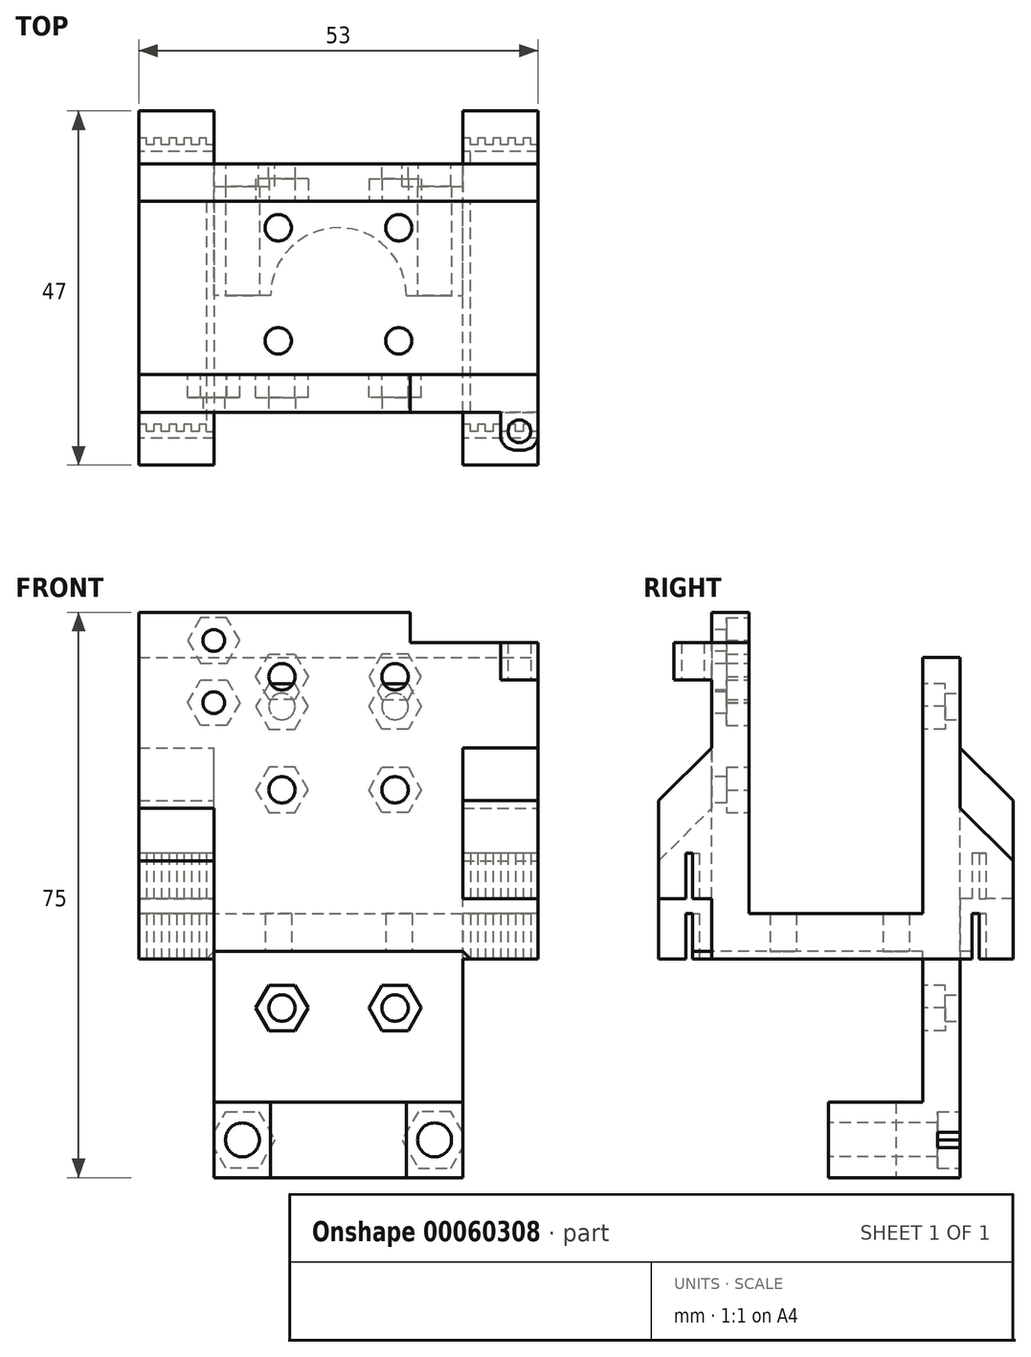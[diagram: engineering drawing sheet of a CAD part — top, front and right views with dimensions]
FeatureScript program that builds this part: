
annotation { "Feature Type Name" : "Feature", "Feature Type Description" : "" }
export const myFeature = defineFeature(function(context is Context, id is Id, definition is map)
    precondition{}
    {
        {
            var Q0;
            Q0=qCreatedBy(makeId("Top.planeOp"),FACE);
            var sketch = newSketch(context, id + "F0", { "sketchPlane" : qUnion([Q0]), "disableImprinting" : false});
            skLineSegment(sketch, "E0.bottom", {"start": v(-26.5, 16) * mm, "end": v(26.5, 16) * mm});
            skLineSegment(sketch, "E0.top", {"start": v(-26.5, -17) * mm, "end": v(26.5, -17) * mm});
            skLineSegment(sketch, "E0.left", {"start": v(-26.5, 16) * mm, "end": v(-26.5, -17) * mm});
            skLineSegment(sketch, "E0.right", {"start": v(26.5, 16) * mm, "end": v(26.5, -17) * mm});
            skLineSegment(sketch, "E1", {"start": v(0, 16) * mm, "end": v(0, -17) * mm, "construction": true});
            skCircle(sketch, "E2", {"center": v(-8, -7.5) * mm, "radius": 1.75 * mm});
            skCircle(sketch, "E3", {"center": v(8, -7.5) * mm, "radius": 1.75 * mm});
            skLineSegment(sketch, "E4", {"start": v(-26.5, -7.5) * mm, "end": v(26.5, -7.5) * mm, "construction": true});
            skLineSegment(sketch, "E5", {"start": v(-26.5, 7.5) * mm, "end": v(26.5, 7.5) * mm, "construction": true});
            skCircle(sketch, "E6", {"center": v(-8, 7.5) * mm, "radius": 1.75 * mm});
            skCircle(sketch, "E7", {"center": v(8, 7.5) * mm, "radius": 1.75 * mm});
            skLineSegment(sketch, "E8", {"start": v(26.5, -0.5) * mm, "end": v(-26.5, -0.5) * mm, "construction": true});
            skLineSegment(sketch, "E9", {"start": v(8, 16) * mm, "end": v(8, -17) * mm, "construction": true});
            skLineSegment(sketch, "E10", {"start": v(-8, 16) * mm, "end": v(-8, -17) * mm, "construction": true});
            skSolve(sketch);
        }
        {
            var Q0;
            Q0=makeQuery(id+"F0.imprint","IMPRINT",FACE,{"disambiguationData":[TD([[makeQuery(id+"F0.imprint","IMPRINT",EDGE,{"derivedFrom":sQuery(id+"F0.wireOp",EDGE,"E0.bottom")}),-1.0]])]});
            extrude(context, id + "F1", {"entities" : qUnion([Q0]), "depth" : 5 * mm});
        }
        {
            var Q0;
            Q0=makeQuery(id+"F1.opExtrude","CAP_FACE",FACE,{"disambiguationData":[OSD([sQuery(id+"F0.wireOp",EDGE,"E0.bottom"),sQuery(id+"F0.wireOp",EDGE,"E0.top"),sQuery(id+"F0.wireOp",EDGE,"E0.left"),sQuery(id+"F0.wireOp",EDGE,"E0.right"),sQuery(id+"F0.wireOp",EDGE,"E2"),sQuery(id+"F0.wireOp",EDGE,"E3"),sQuery(id+"F0.wireOp",EDGE,"E6"),sQuery(id+"F0.wireOp",EDGE,"E7")])],"isStart":false});
            var sketch = newSketch(context, id + "F2", { "sketchPlane" : qUnion([Q0])});
            skLineSegment(sketch, "E11.bottom", {"start": v(-26.5, 16) * mm, "end": v(26.5, 16) * mm});
            skLineSegment(sketch, "E11.top", {"start": v(-26.5, 11) * mm, "end": v(26.5, 11) * mm});
            skLineSegment(sketch, "E11.left", {"start": v(-26.5, 16) * mm, "end": v(-26.5, 11) * mm});
            skLineSegment(sketch, "E11.right", {"start": v(26.5, 16) * mm, "end": v(26.5, 11) * mm});
            skLineSegment(sketch, "E12.MirrorCS", {"start": v(-26.5, -12) * mm, "end": v(26.5, -12) * mm});
            skLineSegment(sketch, "E13.MirrorCS", {"start": v(-26.5, -17) * mm, "end": v(26.5, -17) * mm});
            skLineSegment(sketch, "E14.MirrorCS", {"start": v(26.5, -17) * mm, "end": v(26.5, -12) * mm});
            skLineSegment(sketch, "E15.MirrorCS", {"start": v(-26.5, -17) * mm, "end": v(-26.5, -12) * mm});
            skSolve(sketch);
        }
        {
            var Q0;
            Q0=makeQuery(id+"F2.imprint","IMPRINT",FACE,{"disambiguationData":[TD([[makeQuery(id+"F2.imprint","IMPRINT",EDGE,{"derivedFrom":sQuery(id+"F2.wireOp",EDGE,"E12.MirrorCS")}),-1.0]])]});
            extrude(context, id + "F3", {"entities" : qUnion([Q0]), "operationType" : NewBodyOperationType.ADD, "depth" : 40 * mm});
        }
        {
            var Q0;
            Q0=makeQuery(id+"F2.imprint","IMPRINT",FACE,{"disambiguationData":[TD([[makeQuery(id+"F2.imprint","IMPRINT",EDGE,{"derivedFrom":sQuery(id+"F2.wireOp",EDGE,"E11.bottom")}),-1.0]])]});
            extrude(context, id + "F4", {"entities" : qUnion([Q0]), "operationType" : NewBodyOperationType.ADD, "depth" : 34 * mm});
        }
        {
            var Q0;
            Q0=makeQuery(id+"F3.boolean.opBoolean","MERGE",FACE,{"derivedFrom":[makeQuery(id+"F1.opExtrude","SWEPT_FACE",FACE,{"disambiguationData":[OSD([sQuery(id+"F0.wireOp",EDGE,"E0.top")])]}),makeQuery(id+"F3.opExtrude","SWEPT_FACE",FACE,{"disambiguationData":[OSD([sQuery(id+"F2.wireOp",EDGE,"E13.MirrorCS")])]})]});
            var sketch = newSketch(context, id + "F5", { "sketchPlane" : qUnion([Q0])});
            skLineSegment(sketch, "E16.bottom", {"start": v(12.5, 0) * mm, "end": v(-12.5, 0) * mm});
            skLineSegment(sketch, "E16.top", {"start": v(12.5, 40) * mm, "end": v(-12.5, 40) * mm});
            skLineSegment(sketch, "E16.left", {"start": v(12.5, 0) * mm, "end": v(12.5, 40) * mm});
            skLineSegment(sketch, "E16.right", {"start": v(-12.5, 0) * mm, "end": v(-12.5, 40) * mm});
            skCircle(sketch, "E17", {"center": v(7.5, 21.44) * mm, "radius": 1.75 * mm});
            skCircle(sketch, "E18", {"center": v(-7.5, 21.44) * mm, "radius": 1.75 * mm});
            skCircle(sketch, "E19", {"center": v(7.5, 36.44) * mm, "radius": 1.75 * mm});
            skCircle(sketch, "E20", {"center": v(-7.5, 36.44) * mm, "radius": 1.75 * mm});
            skSolve(sketch);
        }
        {
            var Q0;
            Q0=makeQuery(id+"F5.imprint","IMPRINT",FACE,{"disambiguationData":[TD([[makeQuery(id+"F5.imprint","IMPRINT",EDGE,{"derivedFrom":sQuery(id+"F5.wireOp",EDGE,"E20")}),1.0]])]});
            var Q1;
            Q1=makeQuery(id+"F5.imprint","IMPRINT",FACE,{"disambiguationData":[TD([[makeQuery(id+"F5.imprint","IMPRINT",EDGE,{"derivedFrom":sQuery(id+"F5.wireOp",EDGE,"E19")}),1.0]])]});
            var Q2;
            Q2=makeQuery(id+"F5.imprint","IMPRINT",FACE,{"disambiguationData":[TD([[makeQuery(id+"F5.imprint","IMPRINT",EDGE,{"derivedFrom":sQuery(id+"F5.wireOp",EDGE,"E17")}),1.0]])]});
            var Q3;
            Q3=makeQuery(id+"F5.imprint","IMPRINT",FACE,{"disambiguationData":[TD([[makeQuery(id+"F5.imprint","IMPRINT",EDGE,{"derivedFrom":sQuery(id+"F5.wireOp",EDGE,"E18")}),1.0]])]});
            extrude(context, id + "F6", {"entities" : qUnion([Q0, Q1, Q2, Q3]), "operationType" : NewBodyOperationType.REMOVE, "oppositeDirection" : true, "depth" : 5 * mm});
        }
        {
            var Q0;
            Q0=makeQuery(id+"F3.boolean.opBoolean","MERGE",FACE,{"derivedFrom":[makeQuery(id+"F1.opExtrude","SWEPT_FACE",FACE,{"disambiguationData":[OSD([sQuery(id+"F0.wireOp",EDGE,"E0.top")])]}),makeQuery(id+"F3.opExtrude","SWEPT_FACE",FACE,{"disambiguationData":[OSD([sQuery(id+"F2.wireOp",EDGE,"E13.MirrorCS")])]})]});
            var sketch = newSketch(context, id + "F7", { "sketchPlane" : qUnion([Q0])});
            skLineSegment(sketch, "E21.bottom", {"start": v(26.5, 7) * mm, "end": v(16.5, 7) * mm});
            skLineSegment(sketch, "E21.top", {"start": v(26.5, 27) * mm, "end": v(16.5, 27) * mm});
            skLineSegment(sketch, "E21.left", {"start": v(26.5, 7) * mm, "end": v(26.5, 27) * mm});
            skLineSegment(sketch, "E21.right", {"start": v(16.5, 7) * mm, "end": v(16.5, 27) * mm});
            skLineSegment(sketch, "E22", {"start": v(26.5, 10) * mm, "end": v(16.5, 10) * mm, "construction": true});
            skLineSegment(sketch, "E23", {"start": v(26.5, 2) * mm, "end": v(-26.5, 2) * mm, "construction": true});
            skLineSegment(sketch, "E24.bottom", {"start": v(-16.5, -1) * mm, "end": v(-26.5, -1) * mm});
            skLineSegment(sketch, "E24.top", {"start": v(-16.5, 19) * mm, "end": v(-26.5, 19) * mm});
            skLineSegment(sketch, "E24.left", {"start": v(-16.5, -1) * mm, "end": v(-16.5, 19) * mm});
            skLineSegment(sketch, "E24.right", {"start": v(-26.5, -1) * mm, "end": v(-26.5, 19) * mm});
            skSolve(sketch);
        }
        {
            var Q0;
            Q0 = qSketchRegion(id + "F7", true);
            extrude(context, id + "F8", {"entities" : qUnion([Q0]), "operationType" : NewBodyOperationType.ADD, "depth" : 7 * mm});
        }
        {
            var Q0;
            Q0=makeQuery(id+"F4.boolean.opBoolean","MERGE",FACE,{"derivedFrom":[makeQuery(id+"F1.opExtrude","SWEPT_FACE",FACE,{"disambiguationData":[OSD([sQuery(id+"F0.wireOp",EDGE,"E0.bottom")])]}),makeQuery(id+"F4.opExtrude","SWEPT_FACE",FACE,{"disambiguationData":[OSD([sQuery(id+"F2.wireOp",EDGE,"E11.bottom")])]})]});
            var sketch = newSketch(context, id + "F9", { "sketchPlane" : qUnion([Q0])});
            skLineSegment(sketch, "E25.bottom", {"start": v(26.5, 7) * mm, "end": v(16.5, 7) * mm});
            skLineSegment(sketch, "E25.top", {"start": v(26.5, 27) * mm, "end": v(16.5, 27) * mm});
            skLineSegment(sketch, "E25.left", {"start": v(26.5, 7) * mm, "end": v(26.5, 27) * mm});
            skLineSegment(sketch, "E25.right", {"start": v(16.5, 7) * mm, "end": v(16.5, 27) * mm});
            skLineSegment(sketch, "E26", {"start": v(26.5, 10) * mm, "end": v(16.5, 10) * mm, "construction": true});
            skLineSegment(sketch, "E27", {"start": v(30, 2) * mm, "end": v(-30, 2) * mm, "construction": true});
            skLineSegment(sketch, "E28.bottom", {"start": v(-16.5, -1) * mm, "end": v(-26.5, -1) * mm});
            skLineSegment(sketch, "E28.top", {"start": v(-16.5, 19) * mm, "end": v(-26.5, 19) * mm});
            skLineSegment(sketch, "E28.left", {"start": v(-16.5, -1) * mm, "end": v(-16.5, 19) * mm});
            skLineSegment(sketch, "E28.right", {"start": v(-26.5, -1) * mm, "end": v(-26.5, 19) * mm});
            skSolve(sketch);
        }
        {
            var Q0;
            Q0 = qSketchRegion(id + "F9", true);
            extrude(context, id + "F10", {"entities" : qUnion([Q0]), "operationType" : NewBodyOperationType.ADD, "depth" : 7 * mm});
        }
        {
            var Q0;
            Q0=makeQuery(id+"F8.opExtrude","SWEPT_FACE",FACE,{"disambiguationData":[OSD([sQuery(id+"F7.wireOp",EDGE,"E21.bottom")])]});
            var sketch = newSketch(context, id + "F11", { "sketchPlane" : qUnion([Q0])});
            skLineSegment(sketch, "E29", {"start": v(26.5, 18.6) * mm, "end": v(16.5, 18.6) * mm, "construction": true});
            skLineSegment(sketch, "E30", {"start": v(26.5, 18.6) * mm, "end": v(26.5, 20.4) * mm, "construction": true});
            skLineSegment(sketch, "E31", {"start": v(26.5, 20.4) * mm, "end": v(16.5, 20.4) * mm});
            skPoint(sketch, "E32.endSnap0", {"position": v(26.5, 20.5) * mm});
            skLineSegment(sketch, "E33", {"start": v(26.5, 19.5) * mm, "end": v(25.5, 19.5) * mm});
            skLineSegment(sketch, "E34", {"start": v(25.5, 19.5) * mm, "end": v(25.5, 18.6) * mm});
            skLineSegment(sketch, "E35", {"start": v(25.5, 18.6) * mm, "end": v(24.5, 18.6) * mm});
            skLineSegment(sketch, "E36", {"start": v(24.5, 18.6) * mm, "end": v(24.5, 19.5) * mm});
            skLineSegment(sketch, "E37", {"start": v(24.5, 19.5) * mm, "end": v(23.5, 19.5) * mm});
            skLineSegment(sketch, "E38", {"start": v(23.5, 19.5) * mm, "end": v(23.5, 18.6) * mm});
            skLineSegment(sketch, "E39", {"start": v(23.5, 18.6) * mm, "end": v(22.5, 18.6) * mm});
            skLineSegment(sketch, "E40", {"start": v(22.5, 18.6) * mm, "end": v(22.5, 19.5) * mm});
            skLineSegment(sketch, "E41", {"start": v(22.5, 19.5) * mm, "end": v(21.5, 19.5) * mm});
            skLineSegment(sketch, "E42", {"start": v(21.5, 19.5) * mm, "end": v(21.5, 18.6) * mm});
            skLineSegment(sketch, "E43", {"start": v(21.5, 18.6) * mm, "end": v(20.5, 18.6) * mm});
            skLineSegment(sketch, "E44", {"start": v(20.5, 18.6) * mm, "end": v(20.5, 19.5) * mm});
            skLineSegment(sketch, "E45", {"start": v(20.5, 19.5) * mm, "end": v(19.5, 19.5) * mm});
            skLineSegment(sketch, "E46", {"start": v(19.5, 19.5) * mm, "end": v(19.5, 18.6) * mm});
            skLineSegment(sketch, "E47", {"start": v(19.5, 18.6) * mm, "end": v(18.5, 18.6) * mm});
            skLineSegment(sketch, "E48", {"start": v(18.5, 18.6) * mm, "end": v(18.5, 19.5) * mm});
            skLineSegment(sketch, "E49", {"start": v(18.5, 19.5) * mm, "end": v(17.5, 19.5) * mm});
            skLineSegment(sketch, "E50", {"start": v(17.5, 19.5) * mm, "end": v(17.5, 18.6) * mm});
            skLineSegment(sketch, "E51", {"start": v(17.5, 18.6) * mm, "end": v(17.5, 18.6) * mm});
            skLineSegment(sketch, "E52", {"start": v(17.5, 18.6) * mm, "end": v(17.5, 19.5) * mm});
            skLineSegment(sketch, "E53", {"start": v(17.5, 18.6) * mm, "end": v(16.5, 18.6) * mm});
            skLineSegment(sketch, "E54", {"start": v(16.5, 18.6) * mm, "end": v(16.5, 19.6) * mm});
            skSolve(sketch);
        }
        {
            var Q0;
            {var subQ2=sQuery(id+"F11.wireOp",EDGE,"E31");Q0=makeQuery(id+"F11.imprint","IMPRINT",FACE,{"disambiguationData":[TD([[makeQuery(id+"F11.imprint","IMPRINT",EDGE,{"derivedFrom":subQ2}),1.0]])]});}
            extrude(context, id + "F12", {"entities" : qUnion([Q0]), "operationType" : NewBodyOperationType.REMOVE, "oppositeDirection" : true, "depth" : 6 * mm});
        }
        {
            var Q0;
            Q0=makeQuery(id+"F10.opExtrude","SWEPT_FACE",FACE,{"disambiguationData":[OSD([sQuery(id+"F9.wireOp",EDGE,"E28.bottom")])]});
            var sketch = newSketch(context, id + "F13", { "sketchPlane" : qUnion([Q0])});
            skLineSegment(sketch, "E55", {"start": v(26.5, -19.4) * mm, "end": v(16.5, -19.4) * mm, "construction": true});
            skLineSegment(sketch, "E56", {"start": v(26.5, -19.4) * mm, "end": v(26.5, -17.6) * mm, "construction": true});
            skLineSegment(sketch, "E57", {"start": v(26.5, -17.6) * mm, "end": v(16.5, -17.6) * mm});
            skPoint(sketch, "E58.endSnap0", {"position": v(30.12, -17.14) * mm});
            skLineSegment(sketch, "E59", {"start": v(26.5, -18.5) * mm, "end": v(25.5, -18.5) * mm});
            skLineSegment(sketch, "E60", {"start": v(25.5, -18.5) * mm, "end": v(25.5, -19.4) * mm});
            skLineSegment(sketch, "E61", {"start": v(25.5, -19.4) * mm, "end": v(24.5, -19.4) * mm});
            skLineSegment(sketch, "E62", {"start": v(24.5, -19.4) * mm, "end": v(24.5, -18.5) * mm});
            skLineSegment(sketch, "E63", {"start": v(24.5, -18.5) * mm, "end": v(23.5, -18.5) * mm});
            skLineSegment(sketch, "E64", {"start": v(23.5, -18.5) * mm, "end": v(23.5, -19.4) * mm});
            skLineSegment(sketch, "E65", {"start": v(23.5, -19.4) * mm, "end": v(22.5, -19.4) * mm});
            skLineSegment(sketch, "E66", {"start": v(22.5, -19.4) * mm, "end": v(22.5, -18.5) * mm});
            skLineSegment(sketch, "E67", {"start": v(22.5, -18.5) * mm, "end": v(21.5, -18.5) * mm});
            skLineSegment(sketch, "E68", {"start": v(21.5, -18.5) * mm, "end": v(21.5, -19.4) * mm});
            skLineSegment(sketch, "E69", {"start": v(21.5, -19.4) * mm, "end": v(20.5, -19.4) * mm});
            skLineSegment(sketch, "E70", {"start": v(20.5, -19.4) * mm, "end": v(20.5, -18.5) * mm});
            skLineSegment(sketch, "E71", {"start": v(20.5, -18.5) * mm, "end": v(19.5, -18.5) * mm});
            skLineSegment(sketch, "E72", {"start": v(19.5, -18.5) * mm, "end": v(19.5, -19.4) * mm});
            skLineSegment(sketch, "E73", {"start": v(19.5, -19.4) * mm, "end": v(18.5, -19.4) * mm});
            skLineSegment(sketch, "E74", {"start": v(18.5, -19.4) * mm, "end": v(18.5, -18.5) * mm});
            skLineSegment(sketch, "E75", {"start": v(18.5, -18.5) * mm, "end": v(17.5, -18.5) * mm});
            skLineSegment(sketch, "E76", {"start": v(17.5, -18.5) * mm, "end": v(17.5, -19.4) * mm});
            skLineSegment(sketch, "E77", {"start": v(17.5, -19.4) * mm, "end": v(17.5, -19.4) * mm});
            skLineSegment(sketch, "E78", {"start": v(17.5, -19.4) * mm, "end": v(17.5, -18.5) * mm});
            skLineSegment(sketch, "E79", {"start": v(17.5, -19.4) * mm, "end": v(16.5, -19.4) * mm});
            skLineSegment(sketch, "E80", {"start": v(16.5, -19.4) * mm, "end": v(16.5, -18.4) * mm});
            skLineSegment(sketch, "E81", {"start": v(16.5, -18.4) * mm, "end": v(16.5, -17.6) * mm});
            skSolve(sketch);
        }
        {
            var Q0;
            Q0=makeQuery(id+"F10.opExtrude","SWEPT_FACE",FACE,{"disambiguationData":[OSD([sQuery(id+"F9.wireOp",EDGE,"E25.bottom")])]});
            var sketch = newSketch(context, id + "F14", { "sketchPlane" : qUnion([Q0])});
            skLineSegment(sketch, "E82", {"start": v(-16.5, -19.4) * mm, "end": v(-26.5, -19.4) * mm, "construction": true});
            skLineSegment(sketch, "E83", {"start": v(-16.5, -19.4) * mm, "end": v(-16.5, -17.6) * mm, "construction": true});
            skLineSegment(sketch, "E84", {"start": v(-16.5, -17.6) * mm, "end": v(-26.5, -17.6) * mm});
            skPoint(sketch, "E85.endSnap0", {"position": v(-19.88, -17.14) * mm});
            skLineSegment(sketch, "E86", {"start": v(-16.5, -18.5) * mm, "end": v(-17.5, -18.5) * mm});
            skLineSegment(sketch, "E87", {"start": v(-17.5, -18.5) * mm, "end": v(-17.5, -19.4) * mm});
            skLineSegment(sketch, "E88", {"start": v(-17.5, -19.4) * mm, "end": v(-18.5, -19.4) * mm});
            skLineSegment(sketch, "E89", {"start": v(-18.5, -19.4) * mm, "end": v(-18.5, -18.5) * mm});
            skLineSegment(sketch, "E90", {"start": v(-18.5, -18.5) * mm, "end": v(-19.5, -18.5) * mm});
            skLineSegment(sketch, "E91", {"start": v(-19.5, -18.5) * mm, "end": v(-19.5, -19.4) * mm});
            skLineSegment(sketch, "E92", {"start": v(-19.5, -19.4) * mm, "end": v(-20.5, -19.4) * mm});
            skLineSegment(sketch, "E93", {"start": v(-20.5, -19.4) * mm, "end": v(-20.5, -18.5) * mm});
            skLineSegment(sketch, "E94", {"start": v(-20.5, -18.5) * mm, "end": v(-21.5, -18.5) * mm});
            skLineSegment(sketch, "E95", {"start": v(-21.5, -18.5) * mm, "end": v(-21.5, -19.4) * mm});
            skLineSegment(sketch, "E96", {"start": v(-21.5, -19.4) * mm, "end": v(-22.5, -19.4) * mm});
            skLineSegment(sketch, "E97", {"start": v(-22.5, -19.4) * mm, "end": v(-22.5, -18.5) * mm});
            skLineSegment(sketch, "E98", {"start": v(-22.5, -18.5) * mm, "end": v(-23.5, -18.5) * mm});
            skLineSegment(sketch, "E99", {"start": v(-23.5, -18.5) * mm, "end": v(-23.5, -19.4) * mm});
            skLineSegment(sketch, "E100", {"start": v(-23.5, -19.4) * mm, "end": v(-24.5, -19.4) * mm});
            skLineSegment(sketch, "E101", {"start": v(-24.5, -19.4) * mm, "end": v(-24.5, -18.5) * mm});
            skLineSegment(sketch, "E102", {"start": v(-24.5, -18.5) * mm, "end": v(-25.5, -18.5) * mm});
            skLineSegment(sketch, "E103", {"start": v(-25.5, -18.5) * mm, "end": v(-25.5, -19.4) * mm});
            skLineSegment(sketch, "E104", {"start": v(-25.5, -19.4) * mm, "end": v(-25.5, -19.4) * mm});
            skLineSegment(sketch, "E105", {"start": v(-25.5, -19.4) * mm, "end": v(-25.5, -18.5) * mm});
            skLineSegment(sketch, "E106", {"start": v(-25.5, -19.4) * mm, "end": v(-26.5, -19.4) * mm});
            skLineSegment(sketch, "E107", {"start": v(-26.5, -19.4) * mm, "end": v(-26.5, -18.4) * mm});
            skLineSegment(sketch, "E108", {"start": v(-26.5, -18.4) * mm, "end": v(-26.5, -17.6) * mm});
            skSolve(sketch);
        }
        {
            var Q0;
            Q0=makeQuery(id+"F8.opExtrude","SWEPT_FACE",FACE,{"disambiguationData":[OSD([sQuery(id+"F7.wireOp",EDGE,"E24.bottom")])]});
            var sketch = newSketch(context, id + "F15", { "sketchPlane" : qUnion([Q0])});
            skLineSegment(sketch, "E109", {"start": v(-16.5, 18.6) * mm, "end": v(-26.5, 18.6) * mm, "construction": true});
            skLineSegment(sketch, "E110", {"start": v(-16.5, 18.6) * mm, "end": v(-16.5, 20.4) * mm, "construction": true});
            skLineSegment(sketch, "E111", {"start": v(-16.5, 20.4) * mm, "end": v(-26.5, 20.4) * mm});
            skLineSegment(sketch, "E112", {"start": v(-16.5, 19.5) * mm, "end": v(-17.5, 19.5) * mm});
            skLineSegment(sketch, "E113", {"start": v(-17.5, 19.5) * mm, "end": v(-17.5, 18.6) * mm});
            skLineSegment(sketch, "E114", {"start": v(-17.5, 18.6) * mm, "end": v(-18.5, 18.6) * mm});
            skLineSegment(sketch, "E115", {"start": v(-18.5, 18.6) * mm, "end": v(-18.5, 19.5) * mm});
            skLineSegment(sketch, "E116", {"start": v(-18.5, 19.5) * mm, "end": v(-19.5, 19.5) * mm});
            skLineSegment(sketch, "E117", {"start": v(-19.5, 19.5) * mm, "end": v(-19.5, 18.6) * mm});
            skLineSegment(sketch, "E118", {"start": v(-19.5, 18.6) * mm, "end": v(-20.5, 18.6) * mm});
            skLineSegment(sketch, "E119", {"start": v(-20.5, 18.6) * mm, "end": v(-20.5, 19.5) * mm});
            skLineSegment(sketch, "E120", {"start": v(-20.5, 19.5) * mm, "end": v(-21.5, 19.5) * mm});
            skLineSegment(sketch, "E121", {"start": v(-21.5, 19.5) * mm, "end": v(-21.5, 18.6) * mm});
            skLineSegment(sketch, "E122", {"start": v(-21.5, 18.6) * mm, "end": v(-22.5, 18.6) * mm});
            skLineSegment(sketch, "E123", {"start": v(-22.5, 18.6) * mm, "end": v(-22.5, 19.5) * mm});
            skLineSegment(sketch, "E124", {"start": v(-22.5, 19.5) * mm, "end": v(-23.5, 19.5) * mm});
            skLineSegment(sketch, "E125", {"start": v(-23.5, 19.5) * mm, "end": v(-23.5, 18.6) * mm});
            skLineSegment(sketch, "E126", {"start": v(-23.5, 18.6) * mm, "end": v(-24.5, 18.6) * mm});
            skLineSegment(sketch, "E127", {"start": v(-24.5, 18.6) * mm, "end": v(-24.5, 19.5) * mm});
            skLineSegment(sketch, "E128", {"start": v(-24.5, 19.5) * mm, "end": v(-25.5, 19.5) * mm});
            skLineSegment(sketch, "E129", {"start": v(-25.5, 19.5) * mm, "end": v(-25.5, 18.6) * mm});
            skLineSegment(sketch, "E130", {"start": v(-25.5, 18.6) * mm, "end": v(-25.5, 18.6) * mm});
            skLineSegment(sketch, "E131", {"start": v(-25.5, 18.6) * mm, "end": v(-25.5, 19.5) * mm});
            skLineSegment(sketch, "E132", {"start": v(-25.5, 18.6) * mm, "end": v(-26.5, 18.6) * mm});
            skLineSegment(sketch, "E133", {"start": v(-26.5, 18.6) * mm, "end": v(-26.5, 19.6) * mm});
            skSolve(sketch);
        }
        {
            var Q0;
            {var subQ0=sQuery(id+"F15.wireOp",EDGE,"E111");Q0=makeQuery(id+"F15.imprint","IMPRINT",FACE,{"disambiguationData":[TD([[makeQuery(id+"F15.imprint","IMPRINT",EDGE,{"derivedFrom":subQ0}),1.0]])]});}
            extrude(context, id + "F16", {"entities" : qUnion([Q0]), "operationType" : NewBodyOperationType.REMOVE, "oppositeDirection" : true, "depth" : 6 * mm});
        }
        {
            var Q0;
            {var subQ1=sQuery(id+"F13.wireOp",EDGE,"E57");Q0=makeQuery(id+"F13.imprint","IMPRINT",FACE,{"disambiguationData":[TD([[makeQuery(id+"F13.imprint","IMPRINT",EDGE,{"derivedFrom":subQ1}),1.0]])]});}
            extrude(context, id + "F17", {"entities" : qUnion([Q0]), "operationType" : NewBodyOperationType.REMOVE, "oppositeDirection" : true, "depth" : 6 * mm});
        }
        {
            var Q0;
            {var subQ0=sQuery(id+"F14.wireOp",EDGE,"E84");Q0=makeQuery(id+"F14.imprint","IMPRINT",FACE,{"disambiguationData":[TD([[makeQuery(id+"F14.imprint","IMPRINT",EDGE,{"derivedFrom":subQ0}),1.0]])]});}
            extrude(context, id + "F18", {"entities" : qUnion([Q0]), "operationType" : NewBodyOperationType.REMOVE, "oppositeDirection" : true, "depth" : 6 * mm});
        }
        {
            var Q0;
            Q0=makeQuery(id+"F3.boolean.opBoolean","MERGE",FACE,{"derivedFrom":[makeQuery(id+"F1.opExtrude","SWEPT_FACE",FACE,{"disambiguationData":[OSD([sQuery(id+"F0.wireOp",EDGE,"E0.top")])]}),makeQuery(id+"F3.opExtrude","SWEPT_FACE",FACE,{"disambiguationData":[OSD([sQuery(id+"F2.wireOp",EDGE,"E13.MirrorCS")])]})]});
            var sketch = newSketch(context, id + "F19", { "sketchPlane" : qUnion([Q0])});
            skCircle(sketch, "E134", {"center": v(-16.55, 33) * mm, "radius": 1.45 * mm});
            skCircle(sketch, "E135", {"center": v(-16.55, 41.25) * mm, "radius": 1.45 * mm});
            skSolve(sketch);
        }
        {
            var Q0;
            Q0=makeQuery(id+"F19.imprint","IMPRINT",FACE,{"disambiguationData":[TD([[makeQuery(id+"F19.imprint","IMPRINT",EDGE,{"derivedFrom":sQuery(id+"F19.wireOp",EDGE,"E134")}),1.0]])]});
            var Q1;
            {var subQ0=sQuery(id+"F19.wireOp",EDGE,"E135");var subQ1=makeQuery(id+"F3.opExtrude","CAP_EDGE",EDGE,{"disambiguationData":[OSD([sQuery(id+"F2.wireOp",EDGE,"E13.MirrorCS")])],"isStart":false});var subQ2=makeQuery(id+"F19.imprint","INTERSECT",VERTEX,{"disambiguationData":[OD(0.0)],"derivedFrom":[subQ1,subQ0]});Q1=makeQuery(id+"F19.imprint","IMPRINT",FACE,{"disambiguationData":[TD([[makeQuery(id+"F19.imprint","IMPRINT",EDGE,{"disambiguationData":[TD([[subQ2,-1.0]])],"derivedFrom":subQ0}),1.0]])]});}
            var Q2;
            {var subQ0=sQuery(id+"F19.wireOp",EDGE,"E135");var subQ1=makeQuery(id+"F3.opExtrude","CAP_EDGE",EDGE,{"disambiguationData":[OSD([sQuery(id+"F2.wireOp",EDGE,"E13.MirrorCS")])],"isStart":false});var subQ2=makeQuery(id+"F19.imprint","INTERSECT",VERTEX,{"disambiguationData":[OD(0.0)],"derivedFrom":[subQ1,subQ0]});Q2=makeQuery(id+"F19.imprint","IMPRINT",FACE,{"disambiguationData":[TD([[makeQuery(id+"F19.imprint","IMPRINT",EDGE,{"disambiguationData":[TD([[subQ2,1.0]])],"derivedFrom":subQ0}),1.0]])]});}
            extrude(context, id + "F20", {"entities" : qUnion([Q0, Q1, Q2]), "operationType" : NewBodyOperationType.REMOVE, "oppositeDirection" : true, "depth" : 5 * mm});
        }
        {
            var Q0;
            Q0=makeQuery(id+"F10.opExtrude","CAP_EDGE",EDGE,{"disambiguationData":[OSD([sQuery(id+"F9.wireOp",EDGE,"E28.top")])],"isStart":false});
            var Q1;
            Q1=makeQuery(id+"F10.opExtrude","CAP_EDGE",EDGE,{"disambiguationData":[OSD([sQuery(id+"F9.wireOp",EDGE,"E25.top")])],"isStart":false});
            var Q2;
            Q2=makeQuery(id+"F8.opExtrude","CAP_EDGE",EDGE,{"disambiguationData":[OSD([sQuery(id+"F7.wireOp",EDGE,"E21.top")])],"isStart":false});
            var Q3;
            Q3=makeQuery(id+"F8.opExtrude","CAP_EDGE",EDGE,{"disambiguationData":[OSD([sQuery(id+"F7.wireOp",EDGE,"E24.top")])],"isStart":false});
            chamfer(context, id + "F21", {"entities" : qUnion([Q0, Q1, Q2, Q3]), "width" : 7 * mm, "tangentPropagation" : true});
        }
        {
            var Q0;
            Q0=makeQuery(id+"F8.opExtrude","CAP_FACE",FACE,{"disambiguationData":[OSD([sQuery(id+"F7.wireOp",EDGE,"E24.bottom"),sQuery(id+"F7.wireOp",EDGE,"E24.top"),sQuery(id+"F7.wireOp",EDGE,"E24.left"),sQuery(id+"F7.wireOp",EDGE,"E24.right")])],"isStart":true});
            extrude(context, id + "F22", {"entities" : qUnion([Q0]), "operationType" : NewBodyOperationType.ADD, "depth" : 33 * mm});
        }
        {
            var Q0;
            Q0=makeQuery(id+"F10.opExtrude","CAP_FACE",FACE,{"disambiguationData":[OSD([sQuery(id+"F9.wireOp",EDGE,"E28.bottom"),sQuery(id+"F9.wireOp",EDGE,"E28.top"),sQuery(id+"F9.wireOp",EDGE,"E28.left"),sQuery(id+"F9.wireOp",EDGE,"E28.right")])],"isStart":true});
            extrude(context, id + "F23", {"entities" : qUnion([Q0]), "operationType" : NewBodyOperationType.ADD, "depth" : 33 * mm});
        }
        {
            var Q0;
            Q0=makeQuery(id+"F3.boolean.opBoolean","MERGE",FACE,{"derivedFrom":[makeQuery(id+"F1.opExtrude","SWEPT_FACE",FACE,{"disambiguationData":[OSD([sQuery(id+"F0.wireOp",EDGE,"E0.top")])]}),makeQuery(id+"F3.opExtrude","SWEPT_FACE",FACE,{"disambiguationData":[OSD([sQuery(id+"F2.wireOp",EDGE,"E13.MirrorCS")])]})]});
            var sketch = newSketch(context, id + "F24", { "sketchPlane" : qUnion([Q0])});
            skLineSegment(sketch, "E136.bottom", {"start": v(26.5, 45) * mm, "end": v(9.5, 45) * mm});
            skLineSegment(sketch, "E136.top", {"start": v(26.5, 41) * mm, "end": v(9.5, 41) * mm});
            skLineSegment(sketch, "E136.left", {"start": v(26.5, 45) * mm, "end": v(26.5, 41) * mm});
            skLineSegment(sketch, "E136.right", {"start": v(9.5, 45) * mm, "end": v(9.5, 41) * mm});
            skSolve(sketch);
        }
        {
            var Q0;
            Q0 = qSketchRegion(id + "F24", true);
            extrude(context, id + "F25", {"entities" : qUnion([Q0]), "operationType" : NewBodyOperationType.REMOVE, "oppositeDirection" : true, "depth" : 5 * mm});
        }
        {
            var Q0;
            Q0=makeQuery(id+"F3.boolean.opBoolean","MERGE",FACE,{"derivedFrom":[makeQuery(id+"F1.opExtrude","SWEPT_FACE",FACE,{"disambiguationData":[OSD([sQuery(id+"F0.wireOp",EDGE,"E0.top")])]}),makeQuery(id+"F3.opExtrude","SWEPT_FACE",FACE,{"disambiguationData":[OSD([sQuery(id+"F2.wireOp",EDGE,"E13.MirrorCS")])]})]});
            var sketch = newSketch(context, id + "F26", { "sketchPlane" : qUnion([Q0])});
            skLineSegment(sketch, "E137.bottom", {"start": v(26.5, 41) * mm, "end": v(21.5, 41) * mm});
            skLineSegment(sketch, "E137.top", {"start": v(26.5, 36) * mm, "end": v(21.5, 36) * mm});
            skLineSegment(sketch, "E137.left", {"start": v(26.5, 41) * mm, "end": v(26.5, 36) * mm});
            skLineSegment(sketch, "E137.right", {"start": v(21.5, 41) * mm, "end": v(21.5, 36) * mm});
            skSolve(sketch);
        }
        {
            var Q0;
            Q0 = qSketchRegion(id + "F26", true);
            extrude(context, id + "F27", {"entities" : qUnion([Q0]), "operationType" : NewBodyOperationType.ADD, "depth" : 5 * mm});
        }
        {
            var Q0;
            Q0=makeQuery(id+"F27.opExtrude","CAP_EDGE",EDGE,{"disambiguationData":[OSD([sQuery(id+"F26.wireOp",EDGE,"E137.left")])],"isStart":false});
            var Q1;
            Q1=makeQuery(id+"F27.opExtrude","CAP_EDGE",EDGE,{"disambiguationData":[OSD([sQuery(id+"F26.wireOp",EDGE,"E137.right")])],"isStart":false});
            fillet(context, id + "F28", {"entities" : qUnion([Q0, Q1]), "radius" : 2 * mm, "tangentPropagation" : true, "allowEdgeOverflow" : false});
        }
        {
            var Q0;
            Q0=makeQuery(id+"F3.opExtrude","SWEPT_FACE",FACE,{"disambiguationData":[OSD([sQuery(id+"F2.wireOp",EDGE,"E12.MirrorCS")])]});
            var sketch = newSketch(context, id + "F29", { "sketchPlane" : qUnion([Q0])});
            skLineSegment(sketch, "E138", {"start": v(0, 45) * mm, "end": v(0, 7.28) * mm, "construction": true});
            skCircle(sketch, "E139.cCircle", {"center": v(-7.5, 36.44) * mm, "radius": 3 * mm, "construction": true});
            skLineSegment(sketch, "E139.0", {"start": v(-4.04, 36.44) * mm, "end": v(-5.77, 33.44) * mm});
            skLineSegment(sketch, "E139.1", {"start": v(-5.77, 33.44) * mm, "end": v(-9.23, 33.44) * mm});
            skLineSegment(sketch, "E139.2", {"start": v(-9.23, 33.44) * mm, "end": v(-10.96, 36.44) * mm});
            skLineSegment(sketch, "E139.3", {"start": v(-10.96, 36.44) * mm, "end": v(-9.23, 39.44) * mm});
            skLineSegment(sketch, "E139.4", {"start": v(-9.23, 39.44) * mm, "end": v(-5.77, 39.44) * mm});
            skLineSegment(sketch, "E139.5", {"start": v(-5.77, 39.44) * mm, "end": v(-4.04, 36.44) * mm});
            skPoint(sketch, "E139.0.midPoint", {"position": v(-4.9, 34.94) * mm});
            skPoint(sketch, "E140.orphan", {"position": v(-26.5, 23) * mm});
            skCircle(sketch, "E141.MirrorC", {"center": v(7.5, 36.44) * mm, "radius": 3 * mm, "construction": true});
            skLineSegment(sketch, "E142.MirrorCS", {"start": v(9.23, 39.44) * mm, "end": v(5.77, 39.44) * mm});
            skLineSegment(sketch, "E143.MirrorCS", {"start": v(5.77, 39.44) * mm, "end": v(4.04, 36.44) * mm});
            skLineSegment(sketch, "E144.MirrorCS", {"start": v(4.04, 36.44) * mm, "end": v(5.77, 33.44) * mm});
            skLineSegment(sketch, "E145.MirrorCS", {"start": v(5.77, 33.44) * mm, "end": v(9.23, 33.44) * mm});
            skLineSegment(sketch, "E146.MirrorCS", {"start": v(9.23, 33.44) * mm, "end": v(10.96, 36.44) * mm});
            skLineSegment(sketch, "E147.MirrorCS", {"start": v(10.96, 36.44) * mm, "end": v(9.23, 39.44) * mm});
            skLineSegment(sketch, "E148", {"start": v(-7.5, 36.44) * mm, "end": v(-7.5, 21.44) * mm, "construction": true});
            skLineSegment(sketch, "E149", {"start": v(-7.5, 28.94) * mm, "end": v(10.81, 28.94) * mm, "construction": true});
            skCircle(sketch, "E150.MirrorC", {"center": v(7.5, 21.44) * mm, "radius": 3 * mm, "construction": true});
            skLineSegment(sketch, "E151.MirrorCS", {"start": v(9.23, 18.44) * mm, "end": v(5.77, 18.44) * mm});
            skLineSegment(sketch, "E152.MirrorCS", {"start": v(10.96, 21.44) * mm, "end": v(9.23, 18.44) * mm});
            skLineSegment(sketch, "E153.MirrorCS", {"start": v(9.23, 24.44) * mm, "end": v(10.96, 21.44) * mm});
            skLineSegment(sketch, "E154.MirrorCS", {"start": v(5.77, 18.44) * mm, "end": v(4.04, 21.44) * mm});
            skLineSegment(sketch, "E155.MirrorCS", {"start": v(5.77, 24.44) * mm, "end": v(9.23, 24.44) * mm});
            skLineSegment(sketch, "E156.MirrorCS", {"start": v(4.04, 21.44) * mm, "end": v(5.77, 24.44) * mm});
            skLineSegment(sketch, "E157.MirrorCS", {"start": v(-5.77, 18.44) * mm, "end": v(-4.04, 21.44) * mm});
            skLineSegment(sketch, "E158.MirrorCS", {"start": v(-10.96, 21.44) * mm, "end": v(-9.23, 18.44) * mm});
            skLineSegment(sketch, "E159.MirrorCS", {"start": v(-9.23, 18.44) * mm, "end": v(-5.77, 18.44) * mm});
            skPoint(sketch, "E160.MirrorP", {"position": v(-4.9, 22.94) * mm});
            skLineSegment(sketch, "E161.MirrorCS", {"start": v(-9.23, 24.44) * mm, "end": v(-10.96, 21.44) * mm});
            skLineSegment(sketch, "E162.MirrorCS", {"start": v(-4.04, 21.44) * mm, "end": v(-5.77, 24.44) * mm});
            skCircle(sketch, "E163.MirrorC", {"center": v(-7.5, 21.44) * mm, "radius": 3 * mm, "construction": true});
            skLineSegment(sketch, "E164.MirrorCS", {"start": v(-5.77, 24.44) * mm, "end": v(-9.23, 24.44) * mm});
            skLineSegment(sketch, "E165", {"start": v(16.55, 37.12) * mm, "end": v(20.71, 37.12) * mm, "construction": true});
            skLineSegment(sketch, "E166.trimOffspring", {"start": v(16.55, 37.12) * mm, "end": v(16.55, 33) * mm, "construction": true});
            skPoint(sketch, "E167.start.orphan", {"position": v(16.55, 41.25) * mm});
            skCircle(sketch, "E168.cCircle", {"center": v(16.55, 41.25) * mm, "radius": 3 * mm, "construction": true});
            skLineSegment(sketch, "E168.0", {"start": v(14.8, 38.26) * mm, "end": v(13.09, 41.27) * mm});
            skLineSegment(sketch, "E168.1", {"start": v(13.09, 41.27) * mm, "end": v(14.83, 44.26) * mm});
            skLineSegment(sketch, "E168.2", {"start": v(14.83, 44.26) * mm, "end": v(18.3, 44.24) * mm});
            skLineSegment(sketch, "E168.3", {"start": v(18.3, 44.24) * mm, "end": v(20.01, 41.23) * mm});
            skLineSegment(sketch, "E168.4", {"start": v(20.01, 41.23) * mm, "end": v(18.27, 38.24) * mm});
            skLineSegment(sketch, "E168.5", {"start": v(18.27, 38.24) * mm, "end": v(14.8, 38.26) * mm});
            skPoint(sketch, "E168.0.midPoint", {"position": v(13.94, 39.76) * mm});
            skLineSegment(sketch, "E169.MirrorCS", {"start": v(13.09, 32.98) * mm, "end": v(14.83, 30) * mm});
            skLineSegment(sketch, "E170.MirrorCS", {"start": v(18.3, 30) * mm, "end": v(20.01, 33.02) * mm});
            skPoint(sketch, "E171.MirrorP", {"position": v(13.94, 34.49) * mm});
            skPoint(sketch, "E172.MirrorP", {"position": v(16.55, 33) * mm});
            skLineSegment(sketch, "E173.MirrorCS", {"start": v(14.83, 30) * mm, "end": v(18.3, 30) * mm});
            skLineSegment(sketch, "E174.MirrorCS", {"start": v(14.8, 36) * mm, "end": v(13.09, 32.98) * mm});
            skCircle(sketch, "E175.MirrorC", {"center": v(16.55, 33) * mm, "radius": 3 * mm, "construction": true});
            skLineSegment(sketch, "E176.MirrorCS", {"start": v(20.01, 33.02) * mm, "end": v(18.27, 36) * mm});
            skLineSegment(sketch, "E177.MirrorCS", {"start": v(18.27, 36) * mm, "end": v(14.8, 36) * mm});
            skLineSegment(sketch, "E178", {"start": v(7.5, 36.44) * mm, "end": v(0, 36.44) * mm, "construction": true});
            skSolve(sketch);
        }
        {
            var Q0;
            Q0 = qSketchRegion(id + "F29", true);
            extrude(context, id + "F30", {"entities" : qUnion([Q0]), "operationType" : NewBodyOperationType.REMOVE, "oppositeDirection" : true, "depth" : 3 * mm});
        }
        {
            var Q0;
            Q0=makeQuery(id+"F27.opExtrude","SWEPT_FACE",FACE,{"disambiguationData":[OSD([sQuery(id+"F26.wireOp",EDGE,"E137.top")])]});
            var sketch = newSketch(context, id + "F31", { "sketchPlane" : qUnion([Q0])});
            skLineSegment(sketch, "E179", {"start": v(24, 17) * mm, "end": v(24, 22) * mm, "construction": true});
            skLineSegment(sketch, "E180", {"start": v(24, 19.5) * mm, "end": v(21.5, 19.5) * mm, "construction": true});
            skCircle(sketch, "E181", {"center": v(24, 19.5) * mm, "radius": 1.5 * mm});
            skSolve(sketch);
        }
        {
            var Q0;
            Q0 = qSketchRegion(id + "F31", true);
            extrude(context, id + "F32", {"entities" : qUnion([Q0]), "operationType" : NewBodyOperationType.REMOVE, "oppositeDirection" : true, "depth" : 5 * mm});
        }
        {
            var Q0;
            Q0=makeQuery(id+"F1.opExtrude","CAP_FACE",FACE,{"disambiguationData":[OSD([sQuery(id+"F0.wireOp",EDGE,"E0.bottom"),sQuery(id+"F0.wireOp",EDGE,"E0.top"),sQuery(id+"F0.wireOp",EDGE,"E0.left"),sQuery(id+"F0.wireOp",EDGE,"E0.right"),sQuery(id+"F0.wireOp",EDGE,"E2"),sQuery(id+"F0.wireOp",EDGE,"E3"),sQuery(id+"F0.wireOp",EDGE,"E6"),sQuery(id+"F0.wireOp",EDGE,"E7")])],"isStart":true});
            var sketch = newSketch(context, id + "F33", { "sketchPlane" : qUnion([Q0])});
            skLineSegment(sketch, "E182.bottom", {"start": v(-16.5, -16) * mm, "end": v(16.5, -16) * mm});
            skLineSegment(sketch, "E182.top", {"start": v(-16.5, -11) * mm, "end": v(16.5, -11) * mm});
            skLineSegment(sketch, "E182.left", {"start": v(-16.5, -16) * mm, "end": v(-16.5, -11) * mm});
            skLineSegment(sketch, "E182.right", {"start": v(16.5, -16) * mm, "end": v(16.5, -11) * mm});
            skSolve(sketch);
        }
        {
            var Q0;
            Q0 = qSketchRegion(id + "F33", true);
            extrude(context, id + "F34", {"entities" : qUnion([Q0]), "operationType" : NewBodyOperationType.ADD, "depth" : 30 * mm});
        }
        {
            var Q0;
            Q0=makeQuery(id+"F34.opExtrude","SWEPT_FACE",FACE,{"disambiguationData":[OSD([sQuery(id+"F33.wireOp",EDGE,"E182.top")])]});
            var sketch = newSketch(context, id + "F35", { "sketchPlane" : qUnion([Q0])});
            skLineSegment(sketch, "E183.bottom", {"start": v(16.5, -30) * mm, "end": v(-16.5, -30) * mm});
            skLineSegment(sketch, "E183.top", {"start": v(16.5, -20) * mm, "end": v(-16.5, -20) * mm});
            skLineSegment(sketch, "E183.left", {"start": v(16.5, -30) * mm, "end": v(16.5, -20) * mm});
            skLineSegment(sketch, "E183.right", {"start": v(-16.5, -30) * mm, "end": v(-16.5, -20) * mm});
            skSolve(sketch);
        }
        {
            var Q0;
            Q0 = qSketchRegion(id + "F35", true);
            extrude(context, id + "F36", {"entities" : qUnion([Q0]), "operationType" : NewBodyOperationType.ADD, "depth" : 12.5 * mm});
        }
        {
            var Q0;
            Q0=makeQuery(id+"F36.boolean.opBoolean","MERGE",FACE,{"derivedFrom":[makeQuery(id+"F34.opExtrude","CAP_FACE",FACE,{"disambiguationData":[OSD([sQuery(id+"F33.wireOp",EDGE,"E182.bottom"),sQuery(id+"F33.wireOp",EDGE,"E182.top"),sQuery(id+"F33.wireOp",EDGE,"E182.left"),sQuery(id+"F33.wireOp",EDGE,"E182.right")])],"isStart":false}),makeQuery(id+"F36.opExtrude","SWEPT_FACE",FACE,{"disambiguationData":[OSD([sQuery(id+"F35.wireOp",EDGE,"E183.bottom")])]})]});
            var sketch = newSketch(context, id + "F37", { "sketchPlane" : qUnion([Q0])});
            skLineSegment(sketch, "E184.bottom", {"start": v(-16.5, -11) * mm, "end": v(16.5, -11) * mm});
            skLineSegment(sketch, "E184.left", {"start": v(-16.5, -11) * mm, "end": v(-16.5, 7.42) * mm});
            skLineSegment(sketch, "E184.right", {"start": v(16.5, -11) * mm, "end": v(16.5, -4.75) * mm});
            skLineSegment(sketch, "E185", {"start": v(0, 1.5) * mm, "end": v(0, 1.5) * mm});
            skCircle(sketch, "E186", {"center": v(0, 1.5) * mm, "radius": 9 * mm});
            skPoint(sketch, "E187.orphan", {"position": v(-16.5, 7.42) * mm});
            skPoint(sketch, "E188.end.orphan", {"position": v(16.5, -4.75) * mm});
            skLineSegment(sketch, "E189", {"start": v(-16.5, 7.42) * mm, "end": v(-6.78, 7.42) * mm});
            skLineSegment(sketch, "E190", {"start": v(16.5, -4.75) * mm, "end": v(6.48, -4.75) * mm});
            skPoint(sketch, "E191.orphan", {"position": v(-16.5, 25.84) * mm});
            skPoint(sketch, "E192.orphan", {"position": v(16.5, 1.5) * mm});
            skSolve(sketch);
        }
        {
            var Q0;
            Q0=makeQuery(id+"F37.imprint","IMPRINT",FACE,{"disambiguationData":[TD([[makeQuery(id+"F37.imprint","IMPRINT",EDGE,{"derivedFrom":sQuery(id+"F37.wireOp",EDGE,"E186")}),1.0]])]});
            extrude(context, id + "F38", {"entities" : qUnion([Q0]), "operationType" : NewBodyOperationType.REMOVE, "oppositeDirection" : true, "depth" : 10 * mm});
        }
        {
            var Q0;
            {var subQ0=sQuery(id+"F35.wireOp",EDGE,"E183.top");var subQ1=sQuery(id+"F33.wireOp",EDGE,"E182.left");var subQ2=sQuery(id+"F35.wireOp",EDGE,"E183.bottom");var subQ3=sQuery(id+"F35.wireOp",EDGE,"E183.right");Q0=makeQuery(id+"F38.boolean.opBoolean","SPLIT",FACE,{"disambiguationData":[TD([makeQuery(id+"F34.opExtrude","SWEPT_FACE",FACE,{"disambiguationData":[OSD([subQ1])]})])],"derivedFrom":makeQuery(id+"F36.opExtrude","CAP_FACE",FACE,{"disambiguationData":[OSD([subQ2,subQ0,sQuery(id+"F35.wireOp",EDGE,"E183.left"),subQ3])],"isStart":false})});}
            var sketch = newSketch(context, id + "F39", { "sketchPlane" : qUnion([Q0])});
            skLineSegment(sketch, "E193", {"start": v(-16.5, -25) * mm, "end": v(17.04, -25) * mm, "construction": true});
            skPoint(sketch, "E193.endSnap0", {"position": v(-9, -25) * mm});
            skLineSegment(sketch, "E194", {"start": v(-12.75, -20) * mm, "end": v(-12.75, -30) * mm, "construction": true});
            skLineSegment(sketch, "E195.MirrorCS", {"start": v(12.75, -20) * mm, "end": v(12.75, -30) * mm, "construction": true});
            skCircle(sketch, "E196", {"center": v(-12.75, -25) * mm, "radius": 2.25 * mm});
            skCircle(sketch, "E197", {"center": v(12.75, -25) * mm, "radius": 2.25 * mm});
            skSolve(sketch);
        }
        {
            var Q0;
            Q0=makeQuery(id+"F39.imprint","IMPRINT",FACE,{"disambiguationData":[TD([[makeQuery(id+"F39.imprint","IMPRINT",EDGE,{"derivedFrom":sQuery(id+"F39.wireOp",EDGE,"E196")}),1.0]])]});
            var Q1;
            Q1=makeQuery(id+"F39.imprint","IMPRINT",FACE,{"disambiguationData":[TD([[makeQuery(id+"F39.imprint","IMPRINT",EDGE,{"derivedFrom":sQuery(id+"F39.wireOp",EDGE,"E197")}),1.0]])]});
            extrude(context, id + "F40", {"entities" : qUnion([Q0, Q1]), "operationType" : NewBodyOperationType.REMOVE, "oppositeDirection" : true, "depth" : 17.5 * mm});
        }
        {
            var Q0;
            Q0=makeQuery(id+"F34.boolean.opBoolean","MERGE",FACE,{"derivedFrom":[makeQuery(id+"F22.boolean.opBoolean","MERGE",FACE,{"derivedFrom":[makeQuery(id+"F4.boolean.opBoolean","MERGE",FACE,{"derivedFrom":[makeQuery(id+"F1.opExtrude","SWEPT_FACE",FACE,{"disambiguationData":[OSD([sQuery(id+"F0.wireOp",EDGE,"E0.bottom")])]}),makeQuery(id+"F4.opExtrude","SWEPT_FACE",FACE,{"disambiguationData":[OSD([sQuery(id+"F2.wireOp",EDGE,"E11.bottom")])]})]}),makeQuery(id+"F22.opExtrude","CAP_FACE",FACE,{"disambiguationData":[OSD([sQuery(id+"F7.wireOp",EDGE,"E24.bottom"),sQuery(id+"F7.wireOp",EDGE,"E24.top"),sQuery(id+"F7.wireOp",EDGE,"E24.left"),sQuery(id+"F7.wireOp",EDGE,"E24.right")])],"isStart":false})]}),makeQuery(id+"F34.opExtrude","SWEPT_FACE",FACE,{"disambiguationData":[OSD([sQuery(id+"F33.wireOp",EDGE,"E182.bottom")])]})]});
            var sketch = newSketch(context, id + "F41", { "sketchPlane" : qUnion([Q0])});
            skCircle(sketch, "E198.cCircle", {"center": v(-12.75, -25) * mm, "radius": 3.75 * mm, "construction": true});
            skLineSegment(sketch, "E198.0", {"start": v(-10.58, -21.25) * mm, "end": v(-8.42, -25) * mm});
            skLineSegment(sketch, "E198.1", {"start": v(-8.42, -25) * mm, "end": v(-10.58, -28.75) * mm});
            skLineSegment(sketch, "E198.2", {"start": v(-10.58, -28.75) * mm, "end": v(-14.92, -28.75) * mm});
            skLineSegment(sketch, "E198.3", {"start": v(-14.92, -28.75) * mm, "end": v(-17.08, -25) * mm});
            skLineSegment(sketch, "E198.4", {"start": v(-17.08, -25) * mm, "end": v(-14.92, -21.25) * mm});
            skLineSegment(sketch, "E198.5", {"start": v(-14.92, -21.25) * mm, "end": v(-10.58, -21.25) * mm});
            skPoint(sketch, "E198.0.midPoint", {"position": v(-9.5, -23.12) * mm});
            skLineSegment(sketch, "E199", {"start": v(-12.75, -25) * mm, "end": v(12.75, -25) * mm, "construction": true});
            skLineSegment(sketch, "E200", {"start": v(0, -30) * mm, "end": v(0, -25) * mm, "construction": true});
            skLineSegment(sketch, "E201.MirrorCS", {"start": v(14.92, -21.25) * mm, "end": v(10.58, -21.25) * mm});
            skLineSegment(sketch, "E202.MirrorCS", {"start": v(10.58, -28.75) * mm, "end": v(14.92, -28.75) * mm});
            skLineSegment(sketch, "E203.MirrorCS", {"start": v(10.58, -21.25) * mm, "end": v(8.42, -25) * mm});
            skCircle(sketch, "E204.MirrorC", {"center": v(12.75, -25) * mm, "radius": 3.75 * mm, "construction": true});
            skLineSegment(sketch, "E205.MirrorCS", {"start": v(8.42, -25) * mm, "end": v(10.58, -28.75) * mm});
            skLineSegment(sketch, "E206.MirrorCS", {"start": v(17.08, -25) * mm, "end": v(14.92, -21.25) * mm});
            skLineSegment(sketch, "E207.MirrorCS", {"start": v(14.92, -28.75) * mm, "end": v(17.08, -25) * mm});
            skPoint(sketch, "E208.MirrorP", {"position": v(9.5, -23.12) * mm});
            skSolve(sketch);
        }
        {
            var Q0;
            Q0=makeQuery(id+"F41.imprint","IMPRINT",FACE,{"disambiguationData":[TD([[makeQuery(id+"F41.imprint","IMPRINT",EDGE,{"derivedFrom":sQuery(id+"F41.wireOp",EDGE,"E198.0")}),-1.0]])]});
            var Q1;
            {var subQ1=sQuery(id+"F41.wireOp",EDGE,"E201.MirrorCS");Q1=makeQuery(id+"F41.imprint","IMPRINT",FACE,{"disambiguationData":[TD([[makeQuery(id+"F41.imprint","IMPRINT",EDGE,{"derivedFrom":subQ1}),1.0]])]});}
            extrude(context, id + "F42", {"entities" : qUnion([Q0, Q1]), "operationType" : NewBodyOperationType.REMOVE, "oppositeDirection" : true, "depth" : 3 * mm});
        }
        {
            var Q0;
            Q0=makeQuery(id+"F34.boolean.opBoolean","MERGE",FACE,{"derivedFrom":[makeQuery(id+"F22.boolean.opBoolean","MERGE",FACE,{"derivedFrom":[makeQuery(id+"F4.boolean.opBoolean","MERGE",FACE,{"derivedFrom":[makeQuery(id+"F1.opExtrude","SWEPT_FACE",FACE,{"disambiguationData":[OSD([sQuery(id+"F0.wireOp",EDGE,"E0.bottom")])]}),makeQuery(id+"F4.opExtrude","SWEPT_FACE",FACE,{"disambiguationData":[OSD([sQuery(id+"F2.wireOp",EDGE,"E11.bottom")])]})]}),makeQuery(id+"F22.opExtrude","CAP_FACE",FACE,{"disambiguationData":[OSD([sQuery(id+"F7.wireOp",EDGE,"E24.bottom"),sQuery(id+"F7.wireOp",EDGE,"E24.top"),sQuery(id+"F7.wireOp",EDGE,"E24.left"),sQuery(id+"F7.wireOp",EDGE,"E24.right")])],"isStart":false})]}),makeQuery(id+"F34.opExtrude","SWEPT_FACE",FACE,{"disambiguationData":[OSD([sQuery(id+"F33.wireOp",EDGE,"E182.bottom")])]})]});
            var sketch = newSketch(context, id + "F43", { "sketchPlane" : qUnion([Q0])});
            skLineSegment(sketch, "E209", {"start": v(-16.5, -15) * mm, "end": v(16.5, -15) * mm, "construction": true});
            skLineSegment(sketch, "E210", {"start": v(-16.5, 0) * mm, "end": v(16.5, 0) * mm, "construction": true});
            skLineSegment(sketch, "E211", {"start": v(-16.5, -7.5) * mm, "end": v(16.5, -7.5) * mm, "construction": true});
            skLineSegment(sketch, "E212", {"start": v(0, -15) * mm, "end": v(0, 0) * mm, "construction": true});
            skCircle(sketch, "E213", {"center": v(-7.5, -7.5) * mm, "radius": 1.75 * mm});
            skCircle(sketch, "E214.MirrorC", {"center": v(7.5, -7.5) * mm, "radius": 1.75 * mm});
            skPoint(sketch, "E215.orphan", {"position": v(0, -30) * mm});
            skSolve(sketch);
        }
        {
            var Q0;
            Q0 = qSketchRegion(id + "F43", true);
            extrude(context, id + "F44", {"entities" : qUnion([Q0]), "operationType" : NewBodyOperationType.REMOVE, "oppositeDirection" : true, "depth" : 5 * mm});
        }
        {
            var Q0;
            Q0=makeQuery(id+"F34.opExtrude","SWEPT_FACE",FACE,{"disambiguationData":[OSD([sQuery(id+"F33.wireOp",EDGE,"E182.top")])]});
            var sketch = newSketch(context, id + "F45", { "sketchPlane" : qUnion([Q0])});
            skCircle(sketch, "E216.cCircle", {"center": v(-7.5, -7.5) * mm, "radius": 3 * mm, "construction": true});
            skLineSegment(sketch, "E216.0", {"start": v(-9.23, -10.5) * mm, "end": v(-10.96, -7.5) * mm});
            skLineSegment(sketch, "E216.1", {"start": v(-10.96, -7.5) * mm, "end": v(-9.23, -4.5) * mm});
            skLineSegment(sketch, "E216.2", {"start": v(-9.23, -4.5) * mm, "end": v(-5.77, -4.5) * mm});
            skLineSegment(sketch, "E216.3", {"start": v(-5.77, -4.5) * mm, "end": v(-4.04, -7.5) * mm});
            skLineSegment(sketch, "E216.4", {"start": v(-4.04, -7.5) * mm, "end": v(-5.77, -10.5) * mm});
            skLineSegment(sketch, "E216.5", {"start": v(-5.77, -10.5) * mm, "end": v(-9.23, -10.5) * mm});
            skPoint(sketch, "E216.0.midPoint", {"position": v(-10.1, -9) * mm});
            skLineSegment(sketch, "E217", {"start": v(0, -20) * mm, "end": v(0, 0) * mm, "construction": true});
            skLineSegment(sketch, "E218.MirrorCS", {"start": v(9.23, -10.5) * mm, "end": v(10.96, -7.5) * mm});
            skLineSegment(sketch, "E219.MirrorCS", {"start": v(4.04, -7.5) * mm, "end": v(5.77, -10.5) * mm});
            skLineSegment(sketch, "E220.MirrorCS", {"start": v(5.77, -4.5) * mm, "end": v(4.04, -7.5) * mm});
            skLineSegment(sketch, "E221.MirrorCS", {"start": v(5.77, -10.5) * mm, "end": v(9.23, -10.5) * mm});
            skPoint(sketch, "E222.MirrorP", {"position": v(10.1, -9) * mm});
            skCircle(sketch, "E223.MirrorC", {"center": v(7.5, -7.5) * mm, "radius": 3 * mm, "construction": true});
            skLineSegment(sketch, "E224.MirrorCS", {"start": v(9.23, -4.5) * mm, "end": v(5.77, -4.5) * mm});
            skLineSegment(sketch, "E225.MirrorCS", {"start": v(10.96, -7.5) * mm, "end": v(9.23, -4.5) * mm});
            skLineSegment(sketch, "E226", {"start": v(-7.5, -7.5) * mm, "end": v(-16.5, -7.5) * mm, "construction": true});
            skSolve(sketch);
        }
        {
            var Q0;
            Q0 = qSketchRegion(id + "F45", true);
            extrude(context, id + "F46", {"entities" : qUnion([Q0]), "operationType" : NewBodyOperationType.REMOVE, "oppositeDirection" : true, "depth" : 3 * mm});
        }
        {
            var Q0;
            Q0=makeQuery(id+"F4.boolean.opBoolean","MERGE",FACE,{"derivedFrom":[makeQuery(id+"F1.opExtrude","SWEPT_FACE",FACE,{"disambiguationData":[OSD([sQuery(id+"F0.wireOp",EDGE,"E0.bottom")])]}),makeQuery(id+"F4.opExtrude","SWEPT_FACE",FACE,{"disambiguationData":[OSD([sQuery(id+"F2.wireOp",EDGE,"E11.bottom")])]})]});
            var sketch = newSketch(context, id + "F47", { "sketchPlane" : qUnion([Q0])});
            skLineSegment(sketch, "E227", {"start": v(-26.5, 32.5) * mm, "end": v(26.5, 32.5) * mm, "construction": true});
            skLineSegment(sketch, "E228", {"start": v(0, 39) * mm, "end": v(0, 0) * mm, "construction": true});
            skCircle(sketch, "E229", {"center": v(7.5, 32.5) * mm, "radius": 1.75 * mm});
            skCircle(sketch, "E230.MirrorC", {"center": v(-7.5, 32.5) * mm, "radius": 1.75 * mm});
            skSolve(sketch);
        }
        {
            var Q0;
            Q0 = qSketchRegion(id + "F47", true);
            extrude(context, id + "F48", {"entities" : qUnion([Q0]), "operationType" : NewBodyOperationType.REMOVE, "oppositeDirection" : true, "depth" : 5 * mm});
        }
        {
            var Q0;
            {var subQ0=sQuery(id+"F9.wireOp",EDGE,"E28.left");var subQ1=makeQuery(id+"F10.opExtrude","SWEPT_FACE",FACE,{"disambiguationData":[OSD([subQ0])]});var subQ2=sQuery(id+"F9.wireOp",EDGE,"E28.bottom");var subQ3=makeQuery(id+"F10.opExtrude","SWEPT_FACE",FACE,{"disambiguationData":[OSD([subQ2])]});var subQ6=makeQuery(id+"F23.opExtrude","SWEPT_FACE",FACE,{"disambiguationData":[OSD([subQ2])]});var subQ7=makeQuery(id+"F23.opExtrude","SWEPT_FACE",FACE,{"disambiguationData":[OSD([subQ0])]});Q0=makeQuery(id+"F34.boolean.opBoolean","SPLIT",EDGE,{"disambiguationData":[topologyDisambiguationEdgeConnected([subQ3,subQ1,subQ6,subQ7]),TD([makeQuery(id+"F1.opExtrude","SWEPT_FACE",FACE,{"disambiguationData":[OSD([sQuery(id+"F0.wireOp",EDGE,"E0.top")])]})])],"derivedFrom":makeQuery(id+"F23.boolean.opBoolean","MERGE",EDGE,{"derivedFrom":[makeQuery(id+"F17.boolean.opBoolean","SPLIT",EDGE,{"disambiguationData":[TD([makeQuery(id+"F17.opExtrude","SWEPT_FACE",FACE,{"disambiguationData":[OSD([sQuery(id+"F13.wireOp",EDGE,"E57")])]})])],"derivedFrom":makeQuery(id+"F10.opExtrude","SWEPT_EDGE",EDGE,{"disambiguationData":[OSD([subQ2,subQ0])]})}),makeQuery(id+"F23.opExtrude","SWEPT_EDGE",EDGE,{"disambiguationData":[OSD([subQ2,subQ0])]})]})});}
            var Q1;
            {var subQ0=sQuery(id+"F7.wireOp",EDGE,"E24.bottom");var subQ2=sQuery(id+"F7.wireOp",EDGE,"E24.left");var subQ3=makeQuery(id+"F8.opExtrude","SWEPT_FACE",FACE,{"disambiguationData":[OSD([subQ2])]});Q1=makeQuery(id+"F34.boolean.opBoolean","SPLIT",EDGE,{"disambiguationData":[topologyDisambiguationEdgeConnected([subQ3])],"derivedFrom":makeQuery(id+"F22.boolean.opBoolean","MERGE",EDGE,{"derivedFrom":[makeQuery(id+"F16.boolean.opBoolean","SPLIT",EDGE,{"disambiguationData":[TD([makeQuery(id+"F16.opExtrude","SWEPT_FACE",FACE,{"disambiguationData":[OSD([sQuery(id+"F15.wireOp",EDGE,"E112")])]})])],"derivedFrom":makeQuery(id+"F8.opExtrude","SWEPT_EDGE",EDGE,{"disambiguationData":[OSD([subQ0,subQ2])]})}),makeQuery(id+"F22.opExtrude","SWEPT_EDGE",EDGE,{"disambiguationData":[OSD([subQ0,subQ2])]})]})});}
            chamfer(context, id + "F49", {"entities" : qUnion([Q0, Q1]), "width" : 1 * mm, "tangentPropagation" : true});
        }
        {
            var Q0;
            Q0=makeQuery(id+"F4.opExtrude","SWEPT_FACE",FACE,{"disambiguationData":[OSD([sQuery(id+"F2.wireOp",EDGE,"E11.top")])]});
            var sketch = newSketch(context, id + "F50", { "sketchPlane" : qUnion([Q0])});
            skLineSegment(sketch, "E231", {"start": v(7.5, 32.5) * mm, "end": v(-7.5, 32.5) * mm, "construction": true});
            skCircle(sketch, "E232.cCircle", {"center": v(7.5, 32.5) * mm, "radius": 3 * mm, "construction": true});
            skLineSegment(sketch, "E232.0", {"start": v(5.77, 35.5) * mm, "end": v(9.23, 35.5) * mm});
            skLineSegment(sketch, "E232.1", {"start": v(9.23, 35.5) * mm, "end": v(10.96, 32.5) * mm});
            skLineSegment(sketch, "E232.2", {"start": v(10.96, 32.5) * mm, "end": v(9.23, 29.5) * mm});
            skLineSegment(sketch, "E232.3", {"start": v(9.23, 29.5) * mm, "end": v(5.77, 29.5) * mm});
            skLineSegment(sketch, "E232.4", {"start": v(5.77, 29.5) * mm, "end": v(4.04, 32.5) * mm});
            skLineSegment(sketch, "E232.5", {"start": v(4.04, 32.5) * mm, "end": v(5.77, 35.5) * mm});
            skPoint(sketch, "E232.0.midPoint", {"position": v(7.5, 35.5) * mm});
            skLineSegment(sketch, "E233", {"start": v(0, 39) * mm, "end": v(0, 32.5) * mm, "construction": true});
            skLineSegment(sketch, "E234.MirrorCS", {"start": v(-10.96, 32.5) * mm, "end": v(-9.23, 29.5) * mm});
            skLineSegment(sketch, "E235.MirrorCS", {"start": v(-9.23, 29.5) * mm, "end": v(-5.77, 29.5) * mm});
            skLineSegment(sketch, "E236.MirrorCS", {"start": v(-4.04, 32.5) * mm, "end": v(-5.77, 35.5) * mm});
            skCircle(sketch, "E237.MirrorC", {"center": v(-7.5, 32.5) * mm, "radius": 3 * mm, "construction": true});
            skLineSegment(sketch, "E238.MirrorCS", {"start": v(-5.77, 35.5) * mm, "end": v(-9.23, 35.5) * mm});
            skPoint(sketch, "E239.MirrorP", {"position": v(-7.5, 35.5) * mm});
            skLineSegment(sketch, "E240.MirrorCS", {"start": v(-5.77, 29.5) * mm, "end": v(-4.04, 32.5) * mm});
            skLineSegment(sketch, "E241.MirrorCS", {"start": v(-9.23, 35.5) * mm, "end": v(-10.96, 32.5) * mm});
            skSolve(sketch);
        }
        {
            var Q0;
            Q0 = qSketchRegion(id + "F50", true);
            extrude(context, id + "F51", {"entities" : qUnion([Q0]), "operationType" : NewBodyOperationType.REMOVE, "oppositeDirection" : true, "depth" : 3 * mm});
        }
    });
